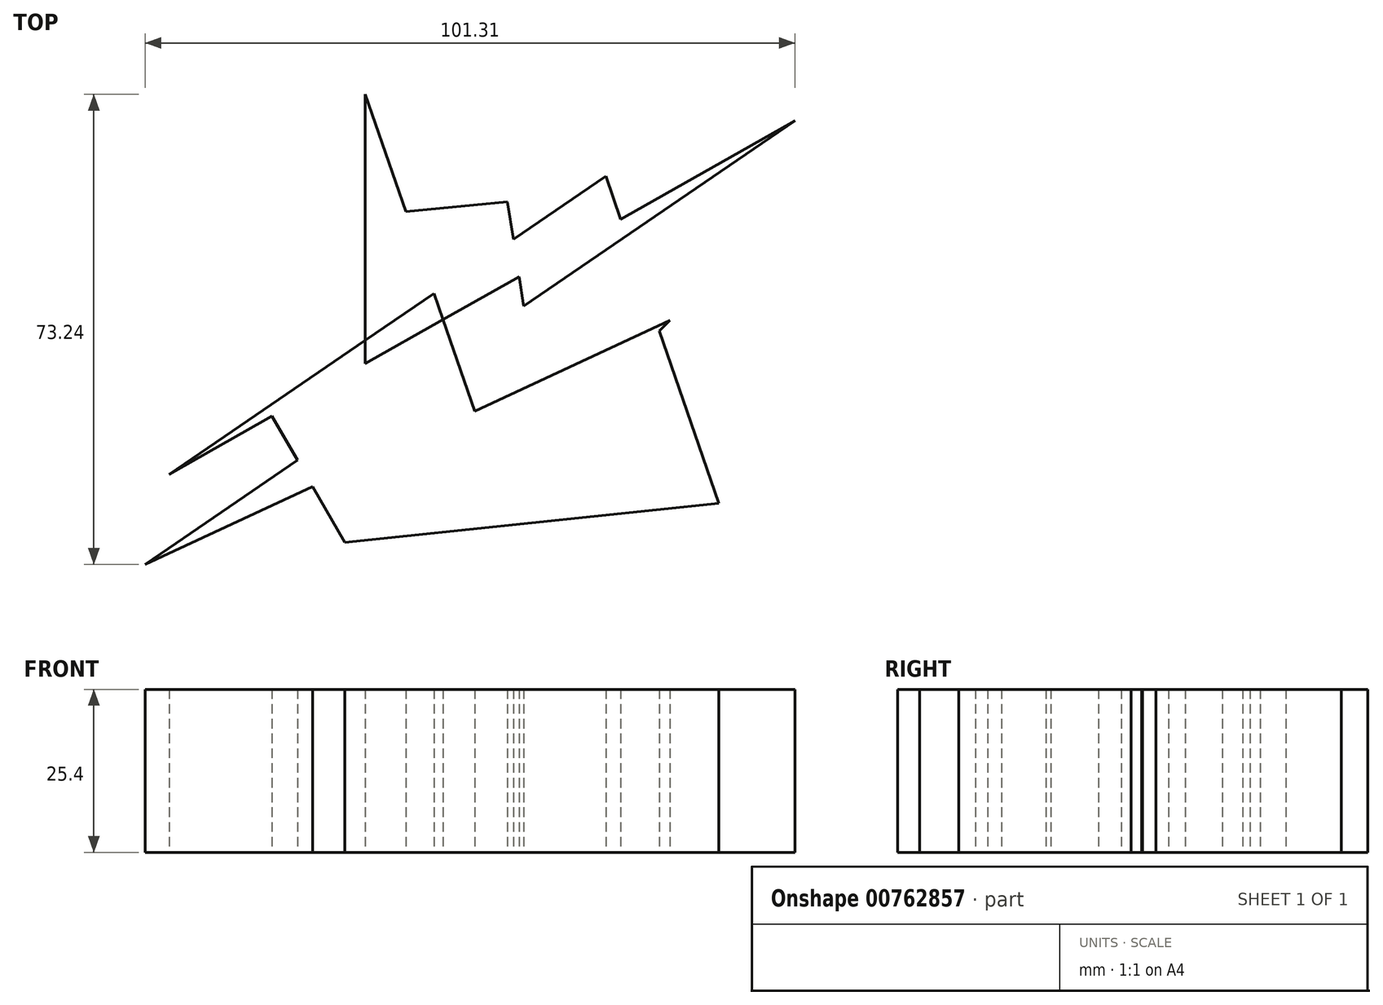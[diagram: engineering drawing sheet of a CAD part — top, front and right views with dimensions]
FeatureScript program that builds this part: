
annotation { "Feature Type Name" : "Feature", "Feature Type Description" : "" }
export const myFeature = defineFeature(function(context is Context, id is Id, definition is map)
    precondition{}
    {
        {
            var Q0;
            Q0=qCreatedBy(makeId("Top.planeOp"),FACE);
            var sketch = newSketch(context, id + "F0", { "sketchPlane" : qUnion([Q0])});
            skLineSegment(sketch, "E0", {"start": v(0, 0) * mm, "end": v(0, 16.71) * mm});
            skLineSegment(sketch, "E1", {"start": v(0, 16.71) * mm, "end": v(0, 51.96) * mm});
            skLineSegment(sketch, "E2", {"start": v(0, 51.96) * mm, "end": v(21.15, -9.3) * mm});
            skLineSegment(sketch, "E3", {"start": v(21.15, -9.3) * mm, "end": v(47.5, 16.71) * mm});
            skLineSegment(sketch, "E4", {"start": v(47.5, 16.71) * mm, "end": v(-34.3, -21.28) * mm});
            skLineSegment(sketch, "E5", {"start": v(-34.3, -21.28) * mm, "end": v(67.01, 47.86) * mm});
            skLineSegment(sketch, "E6", {"start": v(67.01, 47.86) * mm, "end": v(-30.53, -7.25) * mm});
            skLineSegment(sketch, "E7", {"start": v(-30.53, -7.25) * mm, "end": v(37.52, 39.2) * mm});
            skLineSegment(sketch, "E8", {"start": v(37.52, 39.2) * mm, "end": v(55.12, -11.77) * mm});
            skLineSegment(sketch, "E9", {"start": v(55.12, -11.77) * mm, "end": v(-3.15, -17.86) * mm});
            skLineSegment(sketch, "E10", {"start": v(-3.15, -17.86) * mm, "end": v(-30.87, 30.06) * mm});
            skLineSegment(sketch, "E11", {"start": v(-30.87, 30.06) * mm, "end": v(22.18, 35.2) * mm});
            skLineSegment(sketch, "E12", {"start": v(22.18, 35.2) * mm, "end": v(32.44, -30.86) * mm});
            skSolve(sketch);
        }
        {
            var Q0;
            {var subQ0=sQuery(id+"F0.wireOp",EDGE,"E2");var subQ1=sQuery(id+"F0.wireOp",EDGE,"E1");var subQ2=makeQuery(id+"F0.imprint","INTERSECT",VERTEX,{"derivedFrom":[subQ1,subQ0]});Q0=makeQuery(id+"F0.imprint","IMPRINT",FACE,{"disambiguationData":[TD([[makeQuery(id+"F0.imprint","IMPRINT",EDGE,{"disambiguationData":[TD([[subQ2,1.0]])],"derivedFrom":subQ1}),-1.0]])]});}
            var Q1;
            {var subQ0=sQuery(id+"F0.wireOp",EDGE,"E4");var subQ1=sQuery(id+"F0.wireOp",EDGE,"E3");var subQ2=makeQuery(id+"F0.imprint","INTERSECT",VERTEX,{"derivedFrom":[subQ1,subQ0]});Q1=makeQuery(id+"F0.imprint","IMPRINT",FACE,{"disambiguationData":[TD([[makeQuery(id+"F0.imprint","IMPRINT",EDGE,{"disambiguationData":[TD([[subQ2,1.0]])],"derivedFrom":subQ1}),1.0]])]});}
            var Q2;
            {var subQ0=sQuery(id+"F0.wireOp",EDGE,"E5");var subQ1=sQuery(id+"F0.wireOp",EDGE,"E4");var subQ2=makeQuery(id+"F0.imprint","INTERSECT",VERTEX,{"derivedFrom":[subQ1,subQ0]});Q2=makeQuery(id+"F0.imprint","IMPRINT",FACE,{"disambiguationData":[TD([[makeQuery(id+"F0.imprint","IMPRINT",EDGE,{"disambiguationData":[TD([[subQ2,1.0]])],"derivedFrom":subQ1}),-1.0]])]});}
            var Q3;
            {var subQ0=sQuery(id+"F0.wireOp",EDGE,"E6");var subQ1=sQuery(id+"F0.wireOp",EDGE,"E5");var subQ2=makeQuery(id+"F0.imprint","INTERSECT",VERTEX,{"derivedFrom":[subQ1,subQ0]});Q3=makeQuery(id+"F0.imprint","IMPRINT",FACE,{"disambiguationData":[TD([[makeQuery(id+"F0.imprint","IMPRINT",EDGE,{"disambiguationData":[TD([[subQ2,1.0]])],"derivedFrom":subQ1}),1.0]])]});}
            var Q4;
            {var subQ0=sQuery(id+"F0.wireOp",EDGE,"E7");var subQ1=sQuery(id+"F0.wireOp",EDGE,"E6");var subQ2=makeQuery(id+"F0.imprint","INTERSECT",VERTEX,{"derivedFrom":[subQ1,subQ0]});Q4=makeQuery(id+"F0.imprint","IMPRINT",FACE,{"disambiguationData":[TD([[makeQuery(id+"F0.imprint","IMPRINT",EDGE,{"disambiguationData":[TD([[subQ2,1.0]])],"derivedFrom":subQ1}),-1.0]])]});}
            var Q5;
            {var subQ0=sQuery(id+"F0.wireOp",EDGE,"E11");var subQ1=sQuery(id+"F0.wireOp",EDGE,"E2");var subQ2=makeQuery(id+"F0.imprint","INTERSECT",VERTEX,{"derivedFrom":[subQ1,subQ0]});Q5=makeQuery(id+"F0.imprint","IMPRINT",FACE,{"disambiguationData":[TD([[makeQuery(id+"F0.imprint","IMPRINT",EDGE,{"disambiguationData":[TD([[subQ2,-1.0]])],"derivedFrom":subQ1}),1.0]])]});}
            var Q6;
            {var subQ0=sQuery(id+"F0.wireOp",EDGE,"E8");var subQ1=sQuery(id+"F0.wireOp",EDGE,"E3");var subQ2=makeQuery(id+"F0.imprint","INTERSECT",VERTEX,{"derivedFrom":[subQ1,subQ0]});Q6=makeQuery(id+"F0.imprint","IMPRINT",FACE,{"disambiguationData":[TD([[makeQuery(id+"F0.imprint","IMPRINT",EDGE,{"disambiguationData":[TD([[subQ2,1.0]])],"derivedFrom":subQ1}),-1.0]])]});}
            var Q7;
            {var subQ0=sQuery(id+"F0.wireOp",EDGE,"E8");var subQ1=sQuery(id+"F0.wireOp",EDGE,"E6");var subQ2=makeQuery(id+"F0.imprint","INTERSECT",VERTEX,{"derivedFrom":[subQ1,subQ0]});Q7=makeQuery(id+"F0.imprint","IMPRINT",FACE,{"disambiguationData":[TD([[makeQuery(id+"F0.imprint","IMPRINT",EDGE,{"disambiguationData":[TD([[subQ2,-1.0]])],"derivedFrom":subQ1}),-1.0]])]});}
            var Q8;
            {var subQ0=sQuery(id+"F0.wireOp",EDGE,"E5");var subQ1=sQuery(id+"F0.wireOp",EDGE,"E0");var subQ2=makeQuery(id+"F0.imprint","INTERSECT",VERTEX,{"derivedFrom":[subQ1,subQ0]});Q8=makeQuery(id+"F0.imprint","IMPRINT",FACE,{"disambiguationData":[TD([[makeQuery(id+"F0.imprint","IMPRINT",EDGE,{"disambiguationData":[TD([[subQ2,-1.0]])],"derivedFrom":subQ1}),1.0]])]});}
            var Q9;
            {var subQ7=sQuery(id+"F0.wireOp",EDGE,"E2");var subQ9=sQuery(id+"F0.wireOp",EDGE,"E3");var subQ10=makeQuery(id+"F0.imprint","INTERSECT",VERTEX,{"derivedFrom":[subQ7,subQ9]});Q9=makeQuery(id+"F0.imprint","IMPRINT",FACE,{"disambiguationData":[TD([[makeQuery(id+"F0.imprint","IMPRINT",EDGE,{"disambiguationData":[TD([[subQ10,1.0]])],"derivedFrom":subQ7}),-1.0]])]});}
            var Q10;
            {var subQ0=sQuery(id+"F0.wireOp",EDGE,"E6");var subQ1=sQuery(id+"F0.wireOp",EDGE,"E0");var subQ2=makeQuery(id+"F0.imprint","INTERSECT",VERTEX,{"derivedFrom":[subQ1,subQ0]});Q10=makeQuery(id+"F0.imprint","IMPRINT",FACE,{"disambiguationData":[TD([[makeQuery(id+"F0.imprint","IMPRINT",EDGE,{"disambiguationData":[TD([[subQ2,-1.0]])],"derivedFrom":subQ1}),1.0]])]});}
            var Q11;
            {var subQ5=sQuery(id+"F0.wireOp",EDGE,"E0");var subQ7=sQuery(id+"F0.wireOp",EDGE,"E1");var subQ8=makeQuery(id+"F0.imprint","INTERSECT",VERTEX,{"derivedFrom":[subQ5,subQ7]});Q11=makeQuery(id+"F0.imprint","IMPRINT",FACE,{"disambiguationData":[TD([[makeQuery(id+"F0.imprint","IMPRINT",EDGE,{"disambiguationData":[TD([[subQ8,1.0]])],"derivedFrom":subQ5}),-1.0]])]});}
            var Q12;
            {var subQ0=sQuery(id+"F0.wireOp",EDGE,"E7");var subQ1=sQuery(id+"F0.wireOp",EDGE,"E2");var subQ2=makeQuery(id+"F0.imprint","INTERSECT",VERTEX,{"derivedFrom":[subQ1,subQ0]});Q12=makeQuery(id+"F0.imprint","IMPRINT",FACE,{"disambiguationData":[TD([[makeQuery(id+"F0.imprint","IMPRINT",EDGE,{"disambiguationData":[TD([[subQ2,-1.0]])],"derivedFrom":subQ1}),1.0]])]});}
            var Q13;
            {var subQ0=sQuery(id+"F0.wireOp",EDGE,"E8");var subQ1=sQuery(id+"F0.wireOp",EDGE,"E3");var subQ2=makeQuery(id+"F0.imprint","INTERSECT",VERTEX,{"derivedFrom":[subQ1,subQ0]});Q13=makeQuery(id+"F0.imprint","IMPRINT",FACE,{"disambiguationData":[TD([[makeQuery(id+"F0.imprint","IMPRINT",EDGE,{"disambiguationData":[TD([[subQ2,1.0]])],"derivedFrom":subQ1}),1.0]])]});}
            var Q14;
            {var subQ0=sQuery(id+"F0.wireOp",EDGE,"E8");var subQ1=sQuery(id+"F0.wireOp",EDGE,"E5");var subQ2=makeQuery(id+"F0.imprint","INTERSECT",VERTEX,{"derivedFrom":[subQ1,subQ0]});Q14=makeQuery(id+"F0.imprint","IMPRINT",FACE,{"disambiguationData":[TD([[makeQuery(id+"F0.imprint","IMPRINT",EDGE,{"disambiguationData":[TD([[subQ2,1.0]])],"derivedFrom":subQ1}),1.0]])]});}
            var Q15;
            {var subQ0=sQuery(id+"F0.wireOp",EDGE,"E5");var subQ2=sQuery(id+"F0.wireOp",EDGE,"E2");var subQ3=makeQuery(id+"F0.imprint","INTERSECT",VERTEX,{"derivedFrom":[subQ2,subQ0]});Q15=makeQuery(id+"F0.imprint","IMPRINT",FACE,{"disambiguationData":[TD([[makeQuery(id+"F0.imprint","IMPRINT",EDGE,{"disambiguationData":[TD([[subQ3,-1.0]])],"derivedFrom":subQ2}),-1.0]])]});}
            var Q16;
            {var subQ0=sQuery(id+"F0.wireOp",EDGE,"E5");var subQ1=sQuery(id+"F0.wireOp",EDGE,"E0");var subQ2=makeQuery(id+"F0.imprint","INTERSECT",VERTEX,{"derivedFrom":[subQ1,subQ0]});Q16=makeQuery(id+"F0.imprint","IMPRINT",FACE,{"disambiguationData":[TD([[makeQuery(id+"F0.imprint","IMPRINT",EDGE,{"disambiguationData":[TD([[subQ2,-1.0]])],"derivedFrom":subQ1}),-1.0]])]});}
            var Q17;
            {var subQ0=sQuery(id+"F0.wireOp",EDGE,"E3");var subQ1=sQuery(id+"F0.wireOp",EDGE,"E2");var subQ2=makeQuery(id+"F0.imprint","INTERSECT",VERTEX,{"derivedFrom":[subQ1,subQ0]});Q17=makeQuery(id+"F0.imprint","IMPRINT",FACE,{"disambiguationData":[TD([[makeQuery(id+"F0.imprint","IMPRINT",EDGE,{"disambiguationData":[TD([[subQ2,1.0]])],"derivedFrom":subQ1}),1.0]])]});}
            extrude(context, id + "F1", {"entities" : qUnion([Q0, Q1, Q2, Q3, Q4, Q5, Q6, Q7, Q8, Q9, Q10, Q11, Q12, Q13, Q14, Q15, Q16, Q17]), "depth" : 25.4 * mm, "offsetDistance" : 25.4 * mm});
        }
    });
